# Revit family: desiree
name_source: partatom
category: Furniture
revit_build: Autodesk Revit 2015 (Build: 20140903_1530(x64)
units: mm (PartAtom-declared; Revit-internal decimal feet)

## types (2) — shared parameters
BIMobject category = Chairs, Stools & Benches
BOSUseNativeGeometries = 1
Brand url = http://www.swedese.com
Date of publishing = 3/22/2016
Design country = Sweden
Edition number = 1
IFC Classification = Furnishing Element
Manufacturer country = Sweden
Manufacturer name = Swedese
Material main = Steel
Material secondary = Fabric
Nominal height = 890
Nominal width = 630
OmniClass Code = 23-21 11 00
OmniClass Description = Commercial Furniture
Product Guid = 44c76bf8-1074-4300-b39c-8d1698caa59b
Product SKU = 23600
Product data url = https://bimobject.com
Product family = Chairs
Product group = Desir??e
Product name = Desir??e
Product url = http://www.swedese.se
QR code = http://bimobject.com
Technical description = https://static-swedese.s3.amazonaws.com
UNSPSC Code = 56
Uniclass 1.4 Code = L8211
Uniclass 1.4 Description = Furniture
Weight Net (Kg) = 3

## type names (no varying parameters)
- COLOUR - (Black)
- COLOUR - (Grey)

## geometry (parser evidence)
native form markers: Sweep x1
no freeform markers — native parametric forms only
